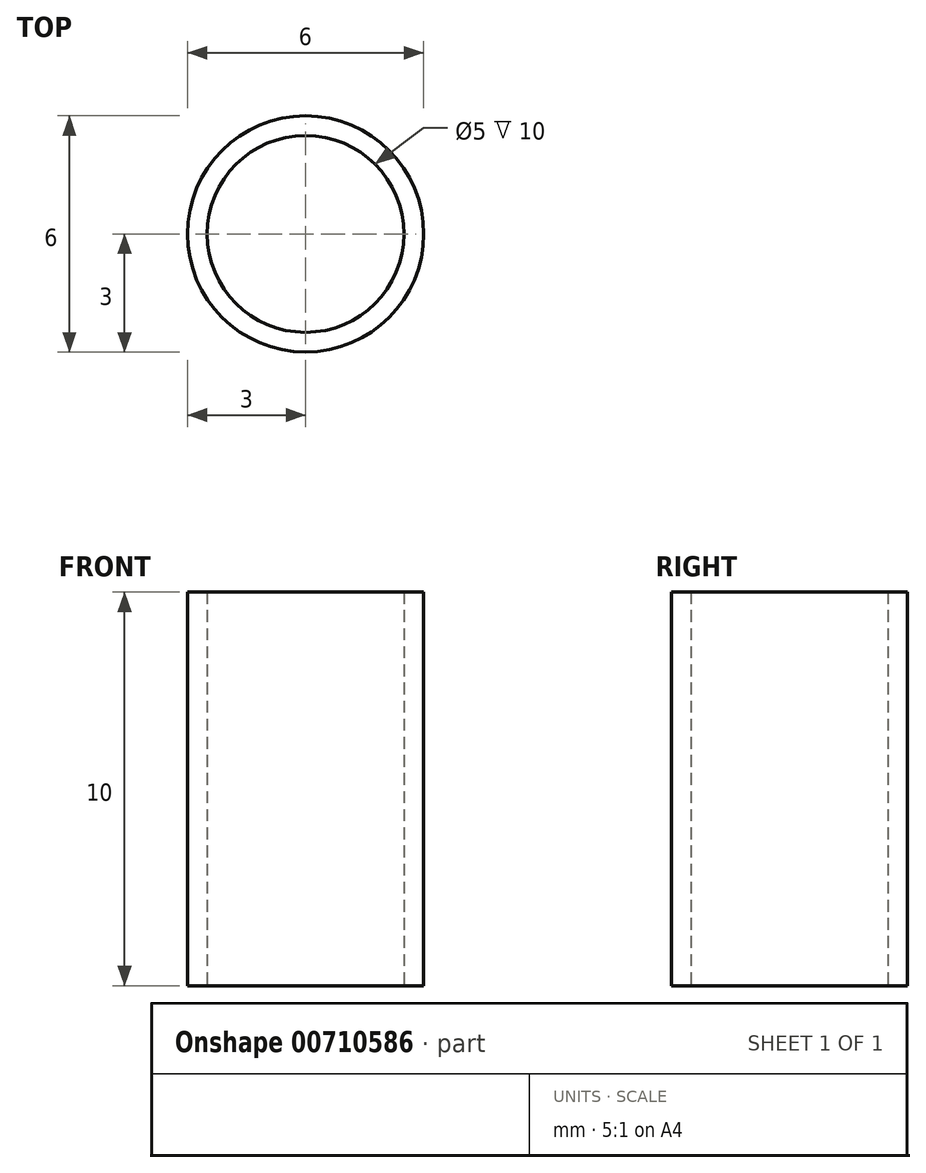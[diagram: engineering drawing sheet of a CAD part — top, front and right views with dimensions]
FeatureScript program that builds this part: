
annotation { "Feature Type Name" : "Feature", "Feature Type Description" : "" }
export const myFeature = defineFeature(function(context is Context, id is Id, definition is map)
    precondition{}
    {
        {
            var Q0;
            Q0=qCreatedBy(makeId("Top.planeOp"),FACE);
            var sketch = newSketch(context, id + "F0", { "sketchPlane" : qUnion([Q0])});
            skCircle(sketch, "E0", {"center": v(0, 0) * mm, "radius": 2.5 * mm});
            skCircle(sketch, "E1", {"center": v(0, 0) * mm, "radius": 3 * mm});
            skSolve(sketch);
        }
        {
            var Q0;
            Q0=makeQuery(id+"F0.imprint","IMPRINT",FACE,{"disambiguationData":[TD([[makeQuery(id+"F0.imprint","IMPRINT",EDGE,{"derivedFrom":sQuery(id+"F0.wireOp",EDGE,"E0")}),-1.0]])]});
            extrude(context, id + "F1", {"entities" : qUnion([Q0]), "depth" : 10 * mm, "offsetDistance" : 25 * mm});
        }
    });
